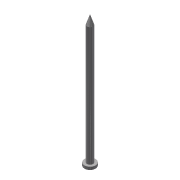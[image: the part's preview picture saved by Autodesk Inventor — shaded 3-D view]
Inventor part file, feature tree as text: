
AUTODESK INVENTOR PART (.ipt)
format: ipt  version: 2016 (Build 200138000, 138)  size: 95,232 bytes
history: native  units: in
note: dims shown in document units (in); Inventor stores cm internally (conversion verified against a paired STEP export)
features: sketch x4, extrude x2, plane x2, revolve x1, fillet x1
ambient origin geometry x8: Origin, YZ Plane, XZ Plane, XY Plane, X Axis, Y Axis, Z Axis, Center Point
bodies: Solid1 (feature_tree)
feature tree (10):
  extrude  "Extrusion1"  Depth=0.1in TaperAngle=0.0deg
  extrude  "Extrusion2"  Depth=4.0in TaperAngle=0.0deg
  sketch  "Sketch3"  dims[d11=-0.096in d12=90.0deg d13=0.02in]
  plane  "Work Plane2"
  revolve  "Revolution1"  Angle=90.0deg
  fillet  "Fillet1"  Radius=0.02in
  sketch  "Sketch1"  dims[d0=0.35in d3=0.1in d4=0.0in]
  sketch  "Sketch2"  dims[d5=0.192in d7=4.0in d8=0.0in]
  plane  "Work Plane1"
  sketch  "Sketch4"
